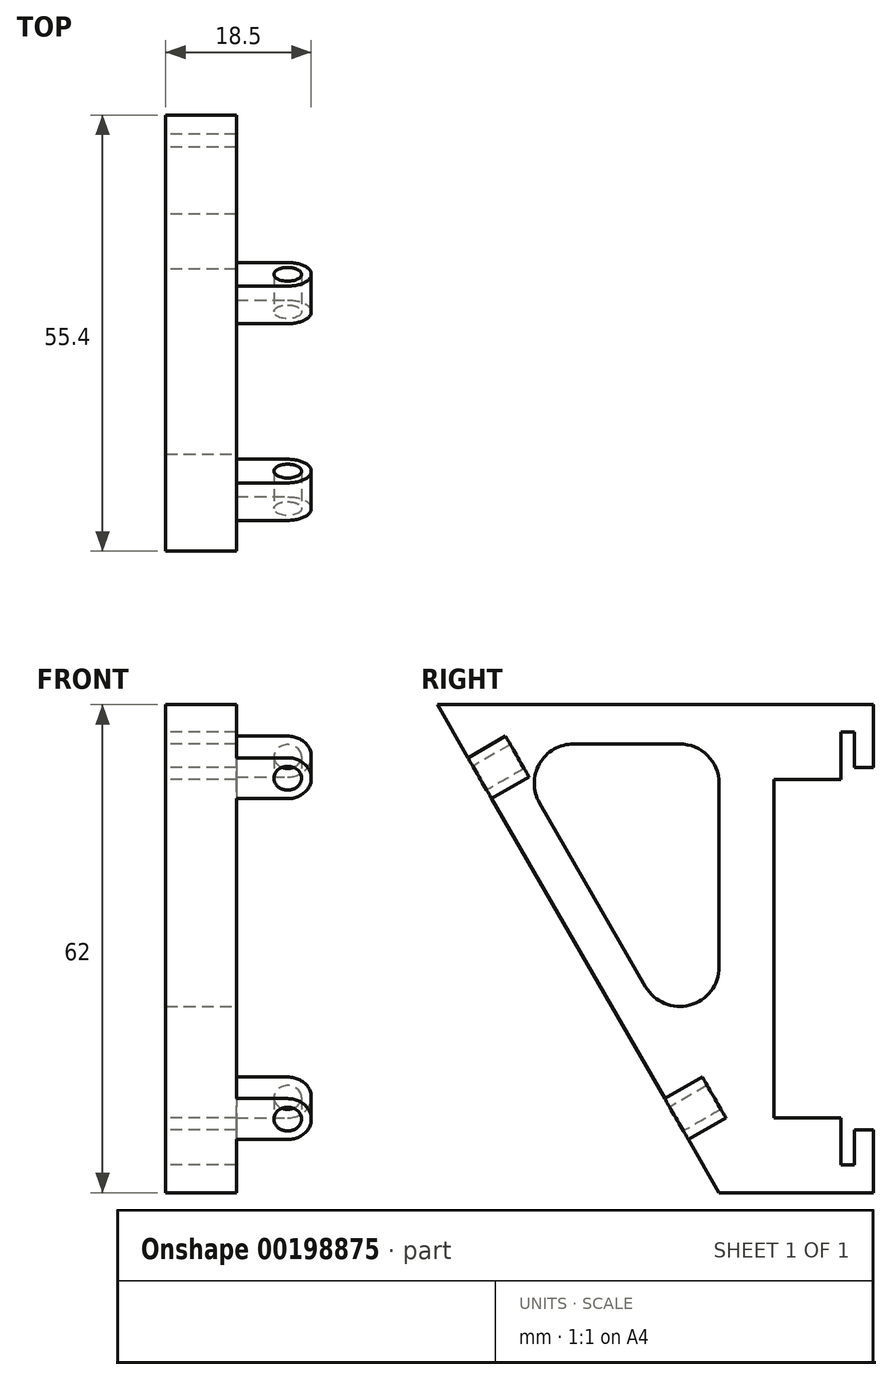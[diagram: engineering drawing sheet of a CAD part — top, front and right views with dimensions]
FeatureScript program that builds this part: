
annotation { "Feature Type Name" : "Feature", "Feature Type Description" : "" }
export const myFeature = defineFeature(function(context is Context, id is Id, definition is map)
    precondition{}
    {
        {
            var Q0;
            Q0=qCreatedBy(makeId("Right.planeOp"),FACE);
            var sketch = newSketch(context, id + "F0", { "sketchPlane" : qUnion([Q0])});
            skLineSegment(sketch, "E0", {"start": v(17.2, 54) * mm, "end": v(19.6, 54) * mm});
            skLineSegment(sketch, "E1", {"start": v(19.6, 54) * mm, "end": v(19.6, 62) * mm});
            skLineSegment(sketch, "E2", {"start": v(19.6, 62) * mm, "end": v(-35.8, 62) * mm});
            skLineSegment(sketch, "E3", {"start": v(-35.8, 62) * mm, "end": v(0, 0) * mm});
            skLineSegment(sketch, "E4", {"start": v(0, 0) * mm, "end": v(19.6, 0) * mm});
            skLineSegment(sketch, "E5", {"start": v(19.6, 0) * mm, "end": v(19.6, 8) * mm});
            skLineSegment(sketch, "E6", {"start": v(19.6, 8) * mm, "end": v(17.2, 8) * mm});
            skLineSegment(sketch, "E7", {"start": v(17.2, 8) * mm, "end": v(17.2, 3.5) * mm});
            skLineSegment(sketch, "E8", {"start": v(17.2, 3.5) * mm, "end": v(15.5, 3.5) * mm});
            skLineSegment(sketch, "E9", {"start": v(15.5, 3.5) * mm, "end": v(15.5, 9.5) * mm});
            skLineSegment(sketch, "E10", {"start": v(15.5, 9.5) * mm, "end": v(7, 9.5) * mm});
            skLineSegment(sketch, "E11", {"start": v(15.5, 58.5) * mm, "end": v(17.2, 58.5) * mm});
            skLineSegment(sketch, "E12", {"start": v(17.2, 58.5) * mm, "end": v(17.2, 54) * mm});
            skLineSegment(sketch, "E13", {"start": v(15.5, 58.5) * mm, "end": v(15.5, 52.5) * mm});
            skLineSegment(sketch, "E14", {"start": v(15.5, 52.5) * mm, "end": v(7, 52.5) * mm});
            skLineSegment(sketch, "E15", {"start": v(7, 9.5) * mm, "end": v(7, 52.5) * mm});
            skLineSegment(sketch, "E16", {"start": v(7, 52.5) * mm, "end": v(7, 62) * mm, "construction": true});
            skLineSegment(sketch, "E17", {"start": v(7, 9.5) * mm, "end": v(7, 0) * mm, "construction": true});
            skLineSegment(sketch, "E18", {"start": v(-27.14, 57) * mm, "end": v(0, 57) * mm});
            skLineSegment(sketch, "E19", {"start": v(0, 57) * mm, "end": v(0, 10) * mm});
            skLineSegment(sketch, "E20", {"start": v(0, 10) * mm, "end": v(-27.14, 57) * mm});
            skLineSegment(sketch, "E21", {"start": v(0, 57) * mm, "end": v(0, 62) * mm, "construction": true});
            skLineSegment(sketch, "E22", {"start": v(-27.14, 57) * mm, "end": v(-31.47, 54.5) * mm, "construction": true});
            skSolve(sketch);
        }
        {
            var Q0;
            Q0 = qSketchRegion(id + "F0", true);
            extrude(context, id + "F1", {"entities" : qUnion([Q0]), "depth" : 9 * mm});
        }
        {
            var Q0;
            Q0=makeQuery(id+"F1.opExtrude","SWEPT_EDGE",EDGE,{"disambiguationData":[OSD([sQuery(id+"F0.wireOp",EDGE,"E18"),sQuery(id+"F0.wireOp",EDGE,"E19")])]});
            var Q1;
            Q1=makeQuery(id+"F1.opExtrude","SWEPT_EDGE",EDGE,{"disambiguationData":[OSD([sQuery(id+"F0.wireOp",EDGE,"E18"),sQuery(id+"F0.wireOp",EDGE,"E20")])]});
            var Q2;
            Q2=makeQuery(id+"F1.opExtrude","SWEPT_EDGE",EDGE,{"disambiguationData":[OSD([sQuery(id+"F0.wireOp",EDGE,"E19"),sQuery(id+"F0.wireOp",EDGE,"E20")])]});
            fillet(context, id + "F2", {"entities" : qUnion([Q0, Q1, Q2]), "radius" : 5 * mm, "tangentPropagation" : true, "allowEdgeOverflow" : false});
        }
        {
            var Q0;
            Q0=makeQuery(id+"F1.opExtrude","SWEPT_FACE",FACE,{"disambiguationData":[OSD([sQuery(id+"F0.wireOp",EDGE,"E3")])]});
            var sketch = newSketch(context, id + "F3", { "sketchPlane" : qUnion([Q0])});
            skLineSegment(sketch, "E23", {"start": v(9, 63.8) * mm, "end": v(15.5, 63.8) * mm});
            skLineSegment(sketch, "E24", {"start": v(9, 63.8) * mm, "end": v(9, 57.8) * mm});
            skLineSegment(sketch, "E25", {"start": v(9, 57.8) * mm, "end": v(15.5, 57.8) * mm});
            skArc(sketch, "E26", {"start": v(15.5, 57.8) * mm, "mid": v(18.5, 60.8) * mm, "end": v(15.5, 63.8) * mm});
            skCircle(sketch, "E27", {"center": v(15.5, 60.8) * mm, "radius": 1.75 * mm});
            skLineSegment(sketch, "E28", {"start": v(8.92, 35.8) * mm, "end": v(9, 35.8) * mm, "construction": true});
            skPoint(sketch, "E28.endSnap0", {"position": v(9, 35.8) * mm});
            skCircle(sketch, "E29.MirrorC", {"center": v(15.5, 10.8) * mm, "radius": 1.75 * mm});
            skLineSegment(sketch, "E30.MirrorCS", {"start": v(9, 13.8) * mm, "end": v(15.5, 13.8) * mm});
            skLineSegment(sketch, "E31.MirrorCS", {"start": v(9, 7.8) * mm, "end": v(15.5, 7.8) * mm});
            skLineSegment(sketch, "E32.MirrorCS", {"start": v(9, 7.8) * mm, "end": v(9, 13.8) * mm});
            skArc(sketch, "E33.MirrorCS", {"start": v(15.5, 13.8) * mm, "mid": v(18.5, 10.8) * mm, "end": v(15.5, 7.8) * mm});
            skSolve(sketch);
        }
        {
            var Q0;
            Q0 = qSketchRegion(id + "F3", true);
            var Q1;
            Q1=makeQuery(id+"F1.opExtrude","SWEPT_FACE",FACE,{"disambiguationData":[OSD([sQuery(id+"F0.wireOp",EDGE,"E20")])]});
            extrude(context, id + "F4", {"entities" : qUnion([Q0]), "operationType" : NewBodyOperationType.ADD, "oppositeDirection" : true, "endBoundEntityFace" : qUnion([Q1]), "depth" : 5.5 * mm});
        }
    });
